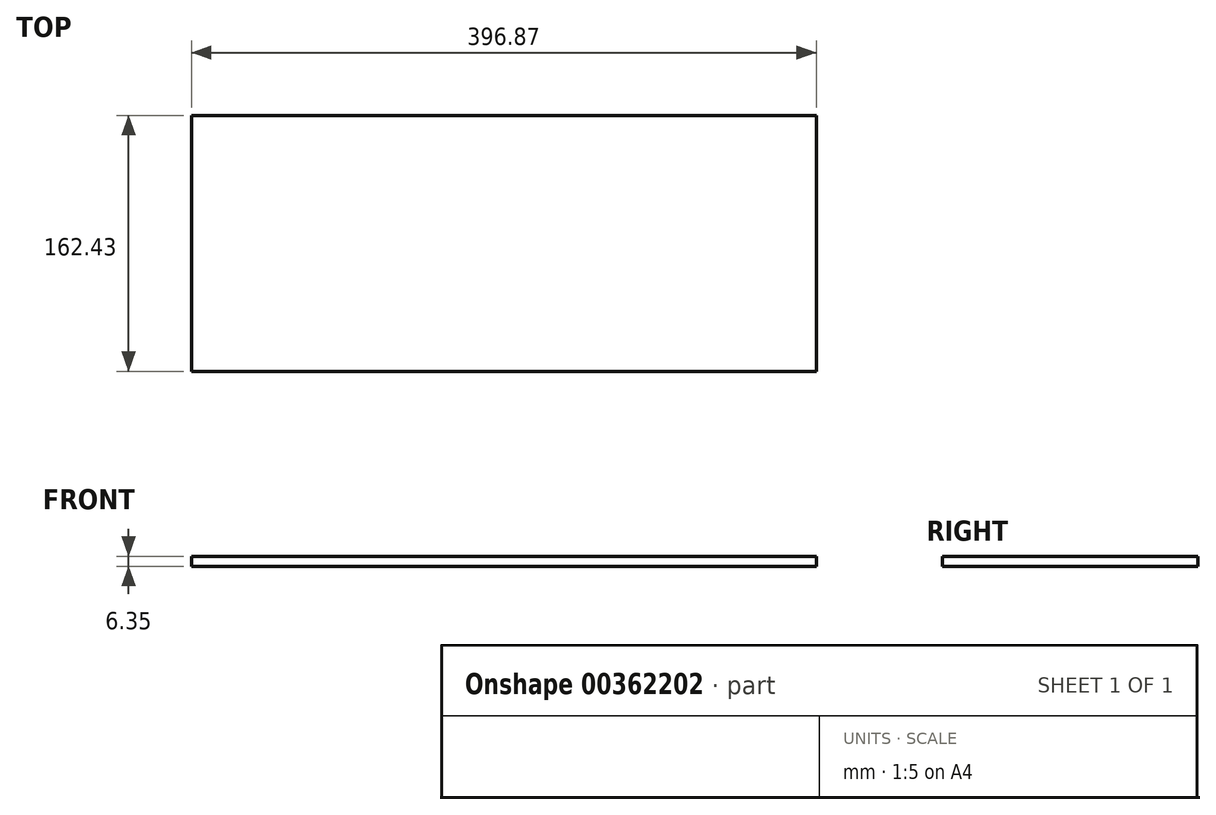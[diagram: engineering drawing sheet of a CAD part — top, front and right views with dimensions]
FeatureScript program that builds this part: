
annotation { "Feature Type Name" : "Feature", "Feature Type Description" : "" }
export const myFeature = defineFeature(function(context is Context, id is Id, definition is map)
    precondition{}
    {
        {
            var Q0;
            Q0=qCreatedBy(makeId("Top.planeOp"),FACE);
            var sketch = newSketch(context, id + "F0", { "sketchPlane" : qUnion([Q0])});
            skLineSegment(sketch, "E0.bottom", {"start": v(122.2, -56.24) * mm, "end": v(519.08, -56.24) * mm});
            skLineSegment(sketch, "E0.top", {"start": v(122.2, 106.2) * mm, "end": v(519.08, 106.2) * mm});
            skLineSegment(sketch, "E0.left", {"start": v(122.2, -56.24) * mm, "end": v(122.2, 106.2) * mm});
            skLineSegment(sketch, "E0.right", {"start": v(519.08, -56.24) * mm, "end": v(519.08, 106.2) * mm});
            skSolve(sketch);
        }
        {
            var Q0;
            Q0 = qSketchRegion(id + "F0", true);
            extrude(context, id + "F1", {"entities" : qUnion([Q0]), "depth" : 6.35 * mm, "offsetDistance" : 25.4 * mm});
        }
    });
